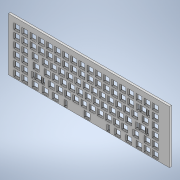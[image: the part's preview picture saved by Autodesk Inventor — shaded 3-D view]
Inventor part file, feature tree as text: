
AUTODESK INVENTOR PART (.ipt)
format: ipt  version: 2020 (Build 240168000, 168)  size: 1,189,376 bytes
history: native  units: mm
features: extrude x4, sketch x4
ambient origin geometry x8: Origin, YZ Plane, XZ Plane, XY Plane, X Axis, Y Axis, Z Axis, Center Point
bodies: Solid1 (feature_tree)
feature tree (8):
  extrude  "Extrusion1"  Depth=5.0mm TaperAngle=0.0deg
  extrude  "Extrusion2"  Depth=9.525mm TaperAngle=0.0deg
  extrude  "Extrusion3"  [1 undecoded]
  extrude  "Extrusion4"  [1 undecoded]
  sketch  "Sketch1"  dims[d0=5.0mm d1=0.0mm d2=23.432mm d3=0.0mm]
  sketch  "Sketch2"  dims[d4=33.338mm d5=9.525mm d6=0.0mm]
  sketch  "Sketch3"  dims[d7=9.906mm d8=0.0mm]
  sketch  "Sketch4"
note: 2 required parameter values undecoded (feature->parameter linkage not recoverable at this tier; creation-order binding heuristic only, values carry confidence <= 0.55)
